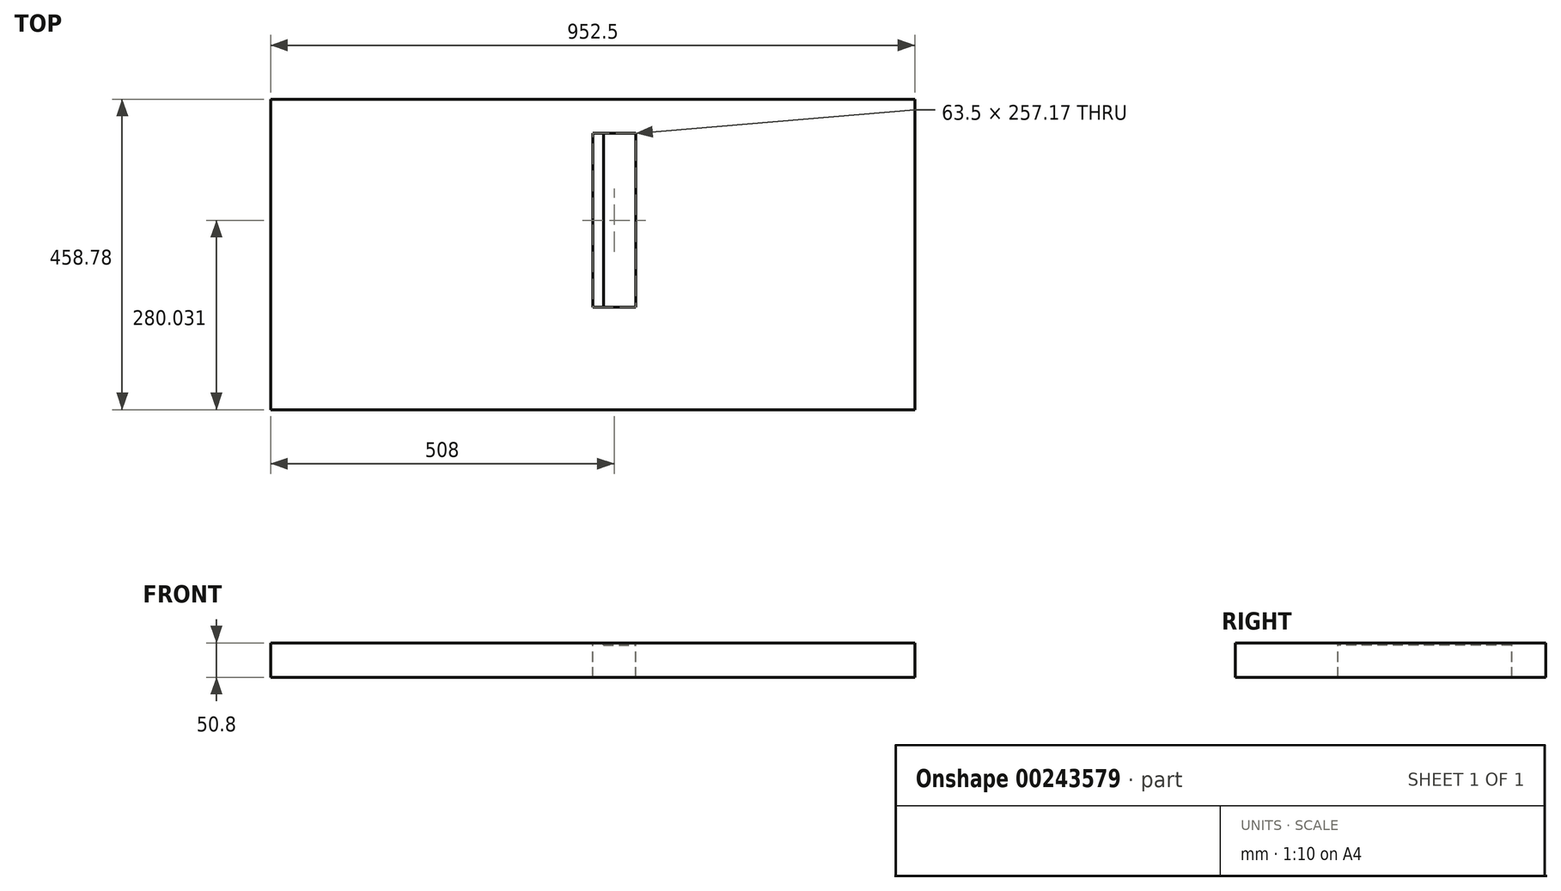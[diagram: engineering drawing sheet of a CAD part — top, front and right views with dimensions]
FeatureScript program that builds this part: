
annotation { "Feature Type Name" : "Feature", "Feature Type Description" : "" }
export const myFeature = defineFeature(function(context is Context, id is Id, definition is map)
    precondition{}
    {
        {
            var Q0;
            Q0=qCreatedBy(makeId("Top.planeOp"),FACE);
            var sketch = newSketch(context, id + "F0", { "sketchPlane" : qUnion([Q0])});
            skLineSegment(sketch, "E0.bottom", {"start": v(476.25, 229.4) * mm, "end": v(-476.25, 229.4) * mm});
            skLineSegment(sketch, "E0.top", {"start": v(476.25, -229.4) * mm, "end": v(-476.25, -229.4) * mm});
            skLineSegment(sketch, "E0.left", {"start": v(476.25, 229.4) * mm, "end": v(476.25, -229.4) * mm});
            skLineSegment(sketch, "E0.right", {"start": v(-476.25, 229.4) * mm, "end": v(-476.25, -229.4) * mm});
            skPoint(sketch, "E0.middle", {"position": v(0, 0) * mm});
            skLineSegment(sketch, "E1.0", {"start": v(63.5, 229.4) * mm, "end": v(63.5, -229.4) * mm, "construction": true});
            skLineSegment(sketch, "E2.0", {"start": v(0, 229.4) * mm, "end": v(0, -229.4) * mm, "construction": true});
            skLineSegment(sketch, "E3.0", {"start": v(476.25, -77.95) * mm, "end": v(-476.25, -77.95) * mm, "construction": true});
            skLineSegment(sketch, "E4.0", {"start": v(476.25, 179.23) * mm, "end": v(-476.25, 179.23) * mm, "construction": true});
            skLineSegment(sketch, "E5", {"start": v(0, 179.23) * mm, "end": v(63.5, 179.23) * mm});
            skLineSegment(sketch, "E6", {"start": v(63.5, 179.23) * mm, "end": v(63.5, -77.95) * mm});
            skLineSegment(sketch, "E7", {"start": v(63.5, -77.95) * mm, "end": v(0, -77.95) * mm});
            skLineSegment(sketch, "E8", {"start": v(0, -77.95) * mm, "end": v(0, 179.23) * mm});
            skSolve(sketch);
        }
        {
            var Q0;
            Q0=makeQuery(id+"F0.imprint","IMPRINT",FACE,{"disambiguationData":[TD([[makeQuery(id+"F0.imprint","IMPRINT",EDGE,{"derivedFrom":sQuery(id+"F0.wireOp",EDGE,"E0.bottom")}),1.0]])]});
            extrude(context, id + "F1", {"entities" : qUnion([Q0]), "oppositeDirection" : true, "depth" : 50.8 * mm});
        }
        {
            var Q0;
            Q0=makeQuery(id+"F1.opExtrude","CAP_FACE",FACE,{"disambiguationData":[OSD([sQuery(id+"F0.wireOp",EDGE,"E0.bottom"),sQuery(id+"F0.wireOp",EDGE,"E0.top"),sQuery(id+"F0.wireOp",EDGE,"E0.left"),sQuery(id+"F0.wireOp",EDGE,"E0.right"),sQuery(id+"F0.wireOp",EDGE,"E5"),sQuery(id+"F0.wireOp",EDGE,"E6"),sQuery(id+"F0.wireOp",EDGE,"E7"),sQuery(id+"F0.wireOp",EDGE,"E8")])],"isStart":true});
            var sketch = newSketch(context, id + "F2", { "sketchPlane" : qUnion([Q0])});
            skLineSegment(sketch, "E9", {"start": v(63.5, 179.23) * mm, "end": v(15.87, 179.23) * mm});
            skLineSegment(sketch, "E10", {"start": v(15.87, 179.23) * mm, "end": v(15.87, -77.95) * mm});
            skLineSegment(sketch, "E11", {"start": v(15.87, -77.95) * mm, "end": v(63.5, -77.95) * mm});
            skLineSegment(sketch, "E12", {"start": v(63.5, -77.95) * mm, "end": v(63.5, 179.23) * mm});
            skSolve(sketch);
        }
        {
            var Q0;
            Q0 = qSketchRegion(id + "F2", true);
            extrude(context, id + "F3", {"entities" : qUnion([Q0]), "oppositeDirection" : true, "depth" : 3.17 * mm});
        }
    });
